# Revit family: Ленточный арочный зенитный фонарь M8CITY_А_ВЕНТ-ДЫМ_со_створками
name_source: partatom
category: Оборудование
revit_build: Autodesk Revit 2017 (Build: 20170118_1100(x64)
units: mm (PartAtom-declared; Revit-internal decimal feet)

## family parameters
Всегда вертикально = Нет
Общий = Нет
Основа = Крыша
При загрузке вырезать с полостями = Нет
Размер круглого соединителя = Использовать диаметр
Тип детали = Нормальный
Точка расчета площади = Нет

## types (1)
- Зенитный фонарь M8CITY Л-А-створки дым/вент
    N арок = 7
    N растров = 8
    URL = www.m8city.by
    Высота = 573 мм
    Высота основания = 500 мм
    Длина = 7800 мм
    Длина ПК = 3415 мм
    Длина проёма = 7800 мм
    Длина проёма ввод = 7800 мм
    Длина створки = 1500 мм
    Изготовитель = ООО Завод М8 Сити Про
    Количество арок = 4
    Количество приводов = 3
    Количество створок = 3
    Количество створок ном = 3
    Количество типовых растров = 7
    Крайний растр = 765 мм
    Описание = Ленточный зенитный фонарь M8CITY в премиальном исполнении со створкой дымоудаления/вентиляции с арочным сводом
    Смещение массива = 1825 мм
    Смещение массива приводов = 1825 мм
    Типовой растр = 1060 мм
    Шаг массива = 2120 мм
    Шаг массива приводов = 2120 мм
    Шаг типовой = 1060 мм
    Ширина = 3000 мм
    Ширина проёма = 3000 мм
    Ширина проёма ввод = 3000 мм
